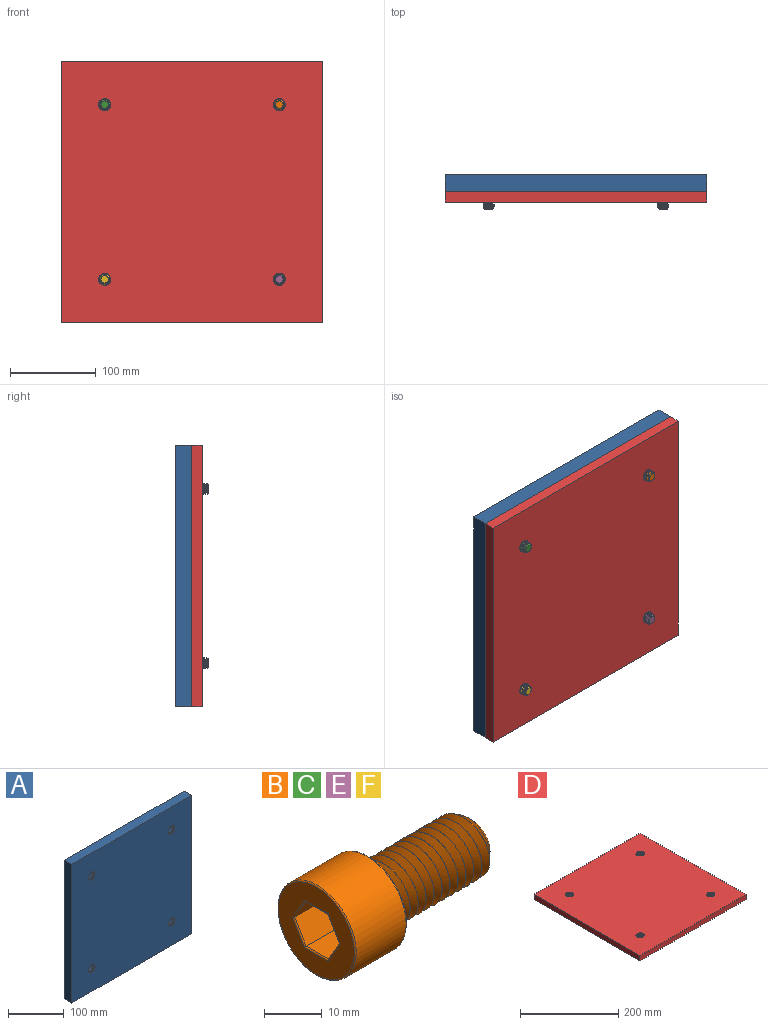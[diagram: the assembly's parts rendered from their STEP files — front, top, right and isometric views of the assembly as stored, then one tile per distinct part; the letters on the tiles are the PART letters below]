
ASSEMBLY  parts=6 mates=5
PART A: 26 faces, bbox 306.2x21.6x306.2 mm
  f0: cylinder r=7.01mm len=14.02mm, axis (0,1,0), area 2.7mm2, adj f8,f16,f24,f25
  f1: cylinder r=7.01mm len=14.02mm, axis (0,1,0), area 2.7mm2, adj f8,f14,f22,f23
  f2: cylinder r=7.01mm len=14.02mm, axis (0,1,0), area 2.7mm2, adj f8,f12,f20,f21
  f3: cylinder r=7.01mm len=14.02mm, axis (0,1,0), area 2.7mm2, adj f8,f10,f18,f19
  f4: plane 304.8x19.05mm, normal (1,0,0), area 5806.4mm2, adj f5,f7,f8,f9
  f5: plane 304.8x19.05mm, normal (0,0,1), area 5806.4mm2, adj f4,f6,f8,f9
  f6: plane 304.8x19.05mm, normal (-1,0,0), area 5806.4mm2, adj f5,f7,f8,f9
  f7: plane 304.8x19.05mm, normal (0,0,-1), area 5806.4mm2, adj f4,f6,f8,f9
  f8: plane 306.18x306.18mm, normal (0,-1,0), area 92128.5mm2, adj f0,f1,f2,f3,f4,f5,f6,f7
  f9: plane 304.8x304.8mm, normal (0,1,0), area 91513.5mm2, adj f4,f5,f6,f7,f11,f13,f15,f17
  f10: plane 22.44x22.44mm, normal (0,1,0), area 153.7mm2, adj f3,f11,f18,f19
  f11: cylinder r=10.52mm len=21.03mm, axis (0,1,0), area 926.4mm2, adj f9,f10
  f12: plane 22.44x22.44mm, normal (0,1,0), area 153.7mm2, adj f2,f13,f20,f21
  f13: cylinder r=10.52mm len=21.03mm, axis (0,1,0), area 926.4mm2, adj f9,f12
  f14: plane 22.44x22.44mm, normal (0,1,0), area 153.7mm2, adj f1,f15,f22,f23
  f15: cylinder r=10.52mm len=21.03mm, axis (0,1,0), area 926.4mm2, adj f9,f14
  f16: plane 22.44x22.44mm, normal (0,1,0), area 153.7mm2, adj f0,f17,f24,f25
  f17: cylinder r=10.52mm len=21.03mm, axis (0,1,0), area 926.4mm2, adj f9,f16
  f18: bspline ~20.05x17.36mm, area 244.9mm2, adj f3,f8,f10,f19
  f19: bspline ~20.05x17.36mm, area 244.9mm2, adj f3,f8,f10,f18
  f20: bspline ~20.05x17.36mm, area 244.9mm2, adj f2,f8,f12,f21
  f21: bspline ~20.05x17.36mm, area 244.9mm2, adj f2,f8,f12,f20
  f22: bspline ~20.05x17.36mm, area 244.9mm2, adj f1,f8,f14,f23
  f23: bspline ~20.05x17.36mm, area 244.9mm2, adj f1,f8,f14,f22
  f24: bspline ~20.05x17.36mm, area 244.9mm2, adj f0,f8,f16,f25
  f25: bspline ~20.05x17.36mm, area 244.9mm2, adj f0,f8,f16,f24
PART B: 24 faces, bbox 39.1x20.6x20.6 mm
  f0: plane 18.54x18.54mm, normal (-1,0,0), area 182.8mm2, adj f16,f17,f18,f19,f20,f21,f23
  f1: cylinder r=6.35mm len=23.45mm, axis (-1,0,0), area 133.2mm2, adj f3,f5,f6,f7,f8
  f2: plane 8.79x8.79mm, normal (1,0,0), area 60.7mm2, adj f5
  f3: plane 18.54x18.54mm, normal (1,0,0), area 143.3mm2, adj f1,f22
  f4: cylinder r=9.53mm len=19.05mm, axis (-1,0,0), area 729.7mm2, adj f22,f23
  f5: cone r=6.35mm half-angle=45deg, axis (-1,0,0), area 50.8mm2, adj f1,f2,f7,f8
  f6: plane 1.93x1.67mm, normal (0,0,-1), area 1.6mm2, adj f1,f7,f8
  f7: bspline ~25.39x14.66mm, area 782.1mm2, adj f1,f5,f6,f8
  f8: bspline ~25.39x14.66mm, area 817mm2, adj f1,f5,f6,f7
  f9: plane 7.87x4.76mm, normal (0,0.87,0.5), area 43.3mm2, adj f10,f14,f15,f17
  f10: plane 7.87x4.76mm, normal (0,0.87,-0.5), area 43.3mm2, adj f9,f11,f15,f16
  f11: plane 7.87x5.5mm, normal (0,0,-1), area 43.3mm2, adj f10,f12,f15,f18
  f12: plane 7.87x4.76mm, normal (0,-0.87,-0.5), area 43.3mm2, adj f11,f13,f15,f20
  f13: plane 7.87x4.76mm, normal (0,-0.87,0.5), area 43.3mm2, adj f12,f14,f15,f21
  f14: plane 7.87x5.5mm, normal (0,0,1), area 43.3mm2, adj f9,f13,f15,f19
  f15: plane 11x9.53mm, normal (-1,0,0), area 78.6mm2, adj f9,f10,f11,f12,f13,f14
  f16: cylinder r=0.25mm len=5.14mm, axis (0,-0.5,-0.87), area 2.3mm2, adj f0,f10,f17,f18
  f17: cylinder r=0.25mm len=5.14mm, axis (0,0.5,-0.87), area 2.3mm2, adj f0,f9,f16,f19
  f18: cylinder r=0.25mm len=5.79mm, axis (0,-1,0), area 2.3mm2, adj f0,f11,f16,f20
  f19: cylinder r=0.25mm len=5.79mm, axis (0,1,0), area 2.3mm2, adj f0,f14,f17,f21
  f20: cylinder r=0.25mm len=5.14mm, axis (0,-0.5,0.87), area 2.3mm2, adj f0,f12,f18,f21
  f21: cylinder r=0.25mm len=5.14mm, axis (0,0.5,0.87), area 2.3mm2, adj f0,f13,f19,f20
  f22: torus R=9.27mm, axis (1,0,0), area 23.6mm2, adj f3,f4
  f23: torus R=9.27mm, axis (-1,0,0), area 23.6mm2, adj f0,f4
PART C: same geometry as B
PART D: 22 faces, bbox 304.8x304.8x14 mm
  f0: cylinder r=7.01mm len=14.02mm, axis (0,0,-1), area 87.7mm2, adj f8,f9,f19,f20,f21
  f1: cylinder r=7.01mm len=14.02mm, axis (0,0,-1), area 87.7mm2, adj f8,f9,f16,f17,f18
  f2: cylinder r=7.01mm len=14.02mm, axis (0,0,-1), area 87.7mm2, adj f8,f9,f13,f14,f15
  f3: cylinder r=7.01mm len=14.02mm, axis (0,0,-1), area 87.7mm2, adj f8,f9,f10,f11,f12
  f4: plane 304.8x12.7mm, normal (0,1,0), area 3871mm2, adj f5,f7,f8,f9
  f5: plane 304.8x12.7mm, normal (-1,0,0), area 3871mm2, adj f4,f6,f8,f9
  f6: plane 304.8x12.7mm, normal (0,-1,0), area 3871mm2, adj f5,f7,f8,f9
  f7: plane 304.8x12.7mm, normal (1,0,0), area 3871mm2, adj f4,f6,f8,f9
  f8: plane 304.8x304.8mm, normal (0,0,1), area 92127.3mm2, adj f0,f1,f2,f3,f4,f5,f6,f7
  f9: plane 304.8x304.8mm, normal (0,0,-1), area 92285.5mm2, adj f0,f1,f2,f3,f4,f5,f6,f7
  f10: plane 1.93x1.67mm, normal (0,1,0), area 1.6mm2, adj f3,f11,f12
  f11: bspline ~20.05x17.36mm, area 598.1mm2, adj f3,f8,f10,f12
  f12: bspline ~20.05x17.36mm, area 549.4mm2, adj f3,f8,f10,f11
  f13: plane 1.93x1.67mm, normal (0,1,0), area 1.6mm2, adj f2,f14,f15
  f14: bspline ~20.05x17.36mm, area 598.1mm2, adj f2,f8,f13,f15
  f15: bspline ~20.05x17.36mm, area 549.4mm2, adj f2,f8,f13,f14
  f16: plane 1.93x1.67mm, normal (0,1,0), area 1.6mm2, adj f1,f17,f18
  f17: bspline ~20.05x17.36mm, area 598.1mm2, adj f1,f8,f16,f18
  f18: bspline ~20.05x17.36mm, area 549.4mm2, adj f1,f8,f16,f17
  f19: plane 1.93x1.67mm, normal (0,1,0), area 1.6mm2, adj f0,f20,f21
  f20: bspline ~20.05x17.36mm, area 598.1mm2, adj f0,f8,f19,f21
  f21: bspline ~20.05x17.36mm, area 549.4mm2, adj f0,f8,f19,f20
PART E: same geometry as B
PART F: same geometry as B
PLACE A t=(-6.47,16.7,276.82)mm
PLACE B rot(axis=(0.58,-0.58,-0.58),120deg) t=(95.13,66.18,73.62)mm
PLACE C rot(axis=(0.58,-0.58,-0.58),120deg) t=(-108.07,66.18,73.62)mm
PLACE D rot(axis=(-1,0,0),90deg) t=(-6.46,-15.05,-27.98)mm
PLACE E rot(axis=(0.58,-0.58,-0.58),120deg) t=(95.13,66.18,-129.58)mm
PLACE F rot(axis=(0.58,-0.58,-0.58),120deg) t=(-108.07,66.18,-129.58)mm
MATE fastened F.f1 <-> A.f1  axis (0,-1,0) through (-108.07,2.68,-129.58)mm
MATE fastened E.f1 <-> A.f0  axis (0,-1,0) through (95.13,2.68,-129.58)mm
MATE fastened B.f1 <-> A.f2  axis (0,-1,0) through (95.13,2.68,73.62)mm
MATE fastened D.f8 <-> A.f8  axis (0,1,0) through (-6.47,-2.35,-27.98)mm
MATE fastened C.f1 <-> A.f3  axis (0,-1,0) through (-108.07,2.68,73.62)mm
